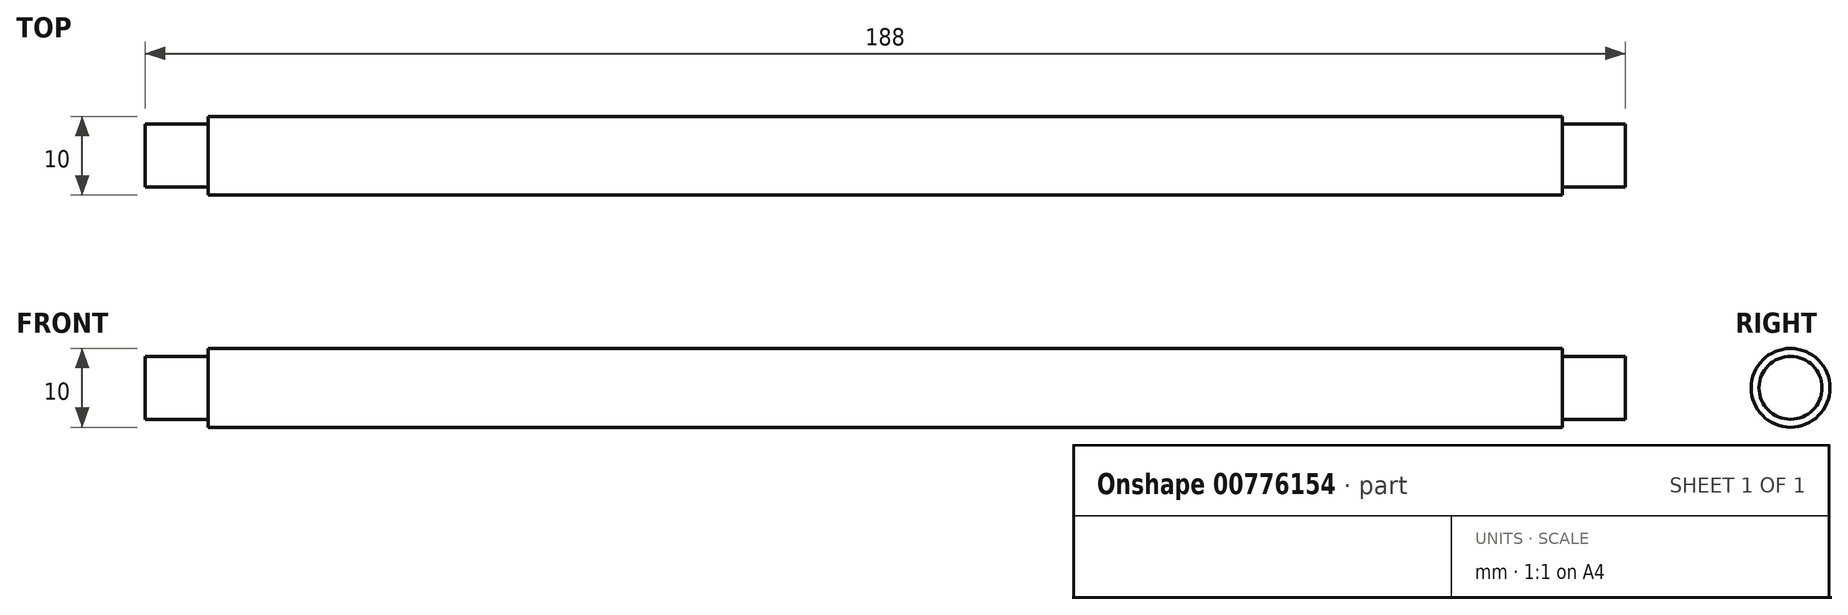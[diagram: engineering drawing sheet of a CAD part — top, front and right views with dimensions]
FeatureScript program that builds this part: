
annotation { "Feature Type Name" : "Feature", "Feature Type Description" : "" }
export const myFeature = defineFeature(function(context is Context, id is Id, definition is map)
    precondition{}
    {
        {
            var Q0;
            Q0=qCreatedBy(makeId("Right.planeOp"),FACE);
            var sketch = newSketch(context, id + "F0", { "sketchPlane" : qUnion([Q0])});
            skCircle(sketch, "E0", {"center": v(0, 0) * mm, "radius": 4 * mm});
            skCircle(sketch, "E1", {"center": v(0, 0) * mm, "radius": 5 * mm});
            skSolve(sketch);
        }
        {
            var Q0;
            Q0=makeQuery(id+"F0.imprint","IMPRINT",FACE,{"disambiguationData":[TD([[makeQuery(id+"F0.imprint","IMPRINT",EDGE,{"derivedFrom":sQuery(id+"F0.wireOp",EDGE,"E0")}),1.0]])]});
            extrude(context, id + "F1", {"entities" : qUnion([Q0]), "depth" : (172 + 16) * mm, "offsetDistance" : 25 * mm, "symmetric" : true});
        }
        {
            var Q0;
            Q0=makeQuery(id+"F0.imprint","IMPRINT",FACE,{"disambiguationData":[TD([[makeQuery(id+"F0.imprint","IMPRINT",EDGE,{"derivedFrom":sQuery(id+"F0.wireOp",EDGE,"E0")}),-1.0]])]});
            extrude(context, id + "F2", {"entities" : qUnion([Q0]), "operationType" : NewBodyOperationType.ADD, "depth" : 172 * mm, "offsetDistance" : 25 * mm, "symmetric" : true});
        }
    });
